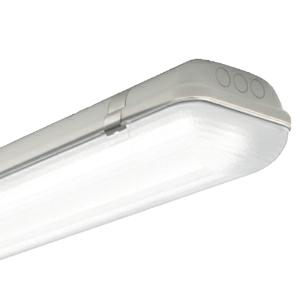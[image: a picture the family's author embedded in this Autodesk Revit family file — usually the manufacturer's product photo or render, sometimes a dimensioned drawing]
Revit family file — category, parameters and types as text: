
# Revit family: 3f_filippi_-_3f_linda_soft_3f_filippi_-_58737_-_3f_linda_led_soft_2x24w_l1270
name_source: partatom
category: Lighting Fixtures
units: mm (PartAtom-declared; Revit-internal decimal feet)

## family parameters
Cut with Voids When Loaded = No
Host = Face
Light Source = No
Part Type = Normal
Room Calculation Point = No
Round Connector Dimension = Use Diameter
Shared = No

## types (1)
- 3F Filippi - 3F Linda Soft (1 x LED, 7156 lm, 54.5 W, 4000 K)
    Apparent Load = 55 VA
    Approval mark = CE
    CIE Flux Codes = 42 72 91 93 100
    Color Rendering = 80
    Color Temperature = 4000 K
    Control Gear = Electronic ballast
    Default Elevation = 1800 mm
    Description = ILLUMINOTECHNICAL
Luminous efficiency 100% (DLOR 93%, ULOR 7%).
Initial luminous flux of the luminaire 7156 lm.
Direct symmetric distribution.
Installation Interdistance Transv.D = 1.35 x hu - Long.D = 1.24 x hu.
Tabular UGR (CIE 117 - 4H-8H; S=0.25H; 70/50/20): RUG 24.6 - 22.6.
Beam angle: 131° - 111°.
Luminous efficacy 131 lm/W.
Lifetime (L93/B10): 30000 h. (tq+25°C)
Lifetime (L90/B10): 50000 h. (tq+25°C)
Lifetime (L85/B10): 80000 h. (tq+25°C)
Lifetime (L80/B10): 100000 h. (tq+25°C)
Lifetime (L85/B10): 50000 h. (tq+35°C)
Sudden decreased luminous flux after 50000 hours: 0% (C0).
Photobiological safety in compliance with IEC/TR 62778: RG0 risk exempt, (IEC 62471).
In compliance with IEC/EN 62722-2-1 - IEC/EN 62717 standards.

SOURCE
2 linear LED modules 24W/840.
Energy efficiency class (UE 2019/2020 - UE 2019/2015): D.
CIE 13.3 Colour rendering index: CRI >80 (R9 <50%).
IES TM-30 Fidelity Index: Rf = 84 Rg = 95.
CCT nominal colour temperature 4000 K.
Colour initial tolerance (MacAdam): SDCM 3.

MECHANICAL
Self-extinguishing V2 polycarbonate housing, injection moulded, RAL 7035 grey.
Ecologic anti-aging injected sealing gasket.
Soft opal diffuser in self-extinguishing V2 polycarbonate, photo-engraved interior, UV stabilised, injection moulded.
Gear-holder reflector in hot-dip galvanised steel, painted with white polyester base.
Snug fit safety snap-lock clips for diffuser mounting in stainless steel, screwdriver opening.
Fixing brackets in stainless steel.
Possibility for technicians to access the interior of the luminaire.
Luminaire with limited surface temperature. - D - (EN 60598-2-24)
Dimensions: 1270x160 mm, height 100 mm. Weight 2.57 kg.
IP66 protection degree.
Mechanical strength to impacts IK10 (20 joule).
Glow-wire test resistance 850°C.

ELECTRICAL
Halogen Free electronic wiring 230V-50/60Hz, power factor 0.97, THD <25%, constant output current, SELV, class I, 1 driver.
Power of the luminaire 54.5 W.
ENEC - CE.
SAFE FLICKER: PstLM=<1 and SVM=<0.4 (IEC TR 61547-1 and IEC TR 63158), to ensure a more comfortable and safe light.
Luminaire compliant with EN 60598-2-22 for power supply from a centralised emergency system CPSS (Central Power Supply System), not incorporated in the luminaire - high risk areas excluded. The default power and flux are 100% in AC and 100% in DC.
Ambient temperature from -20°C to +35°C.
Temperature class T6 max 85°C.
Relative humidity UR: <85%.

INSTALLATION
Ceiling / Suspended / Wall.
All accessories dedicated to this product are available on the Catalog and on our website www.3F-Filippi.com.

APPLICATIONS
Suitable product for food production plants (HACCP), IFS (Food Version 6), BRC (GSFS Food Version 7).
Dry, dusty indoor environments, subject to occasional water splashes.
Luminaires designed for diffuse direct/indirect lighting suitable to provide optimum visual comfort.
Transit areas, stairwells.
Virtually shatterproof polycarbonate compatibly with the fumes / atmospheres that compromise the elasticity of plastic materials.
Suitable for illumination of public car parks and parking grounds referred to DIN 67528:2018-04.

WARNING
Fixture not suitable for cold stores with an ambient temperature <0°C and/or relative humidity >85%.
Luminaire designed for disposal/recycling at end-of-life.
Replaceable (LED only) light source by a professional. Replaceable control gear by a professional.
    Height = 100 mm  [stored 0.328084 ft]
    Lamp = 1 x LED
    Lamp Light Flux = 7156 lm
    Lamp Power = 54.5 W
    Lamp count = 1
    Length = 1270 mm
    Lifetime = 50000 h
    Luminous efficacy = 131 lm/W
    Manufacturer = 3F Filippi
    ModVariant = No
    Model = 3F Filippi - 58737 - 3F Linda LED Soft 2x24W L1270
    Mounting Place = Ceiling
    Mounting Type = Pendant
    Number of Poles = 1
    OnlyDefault = Yes
    Power Factor = 1
    Product Name = 3F Filippi - 3F Linda Soft
    Product group = pendant luminaire
    ProductGroupID = 9
    Protection Class = Protection class I
    Protection Degree = IP 66
    RLX_Detail_Level = 1
    RLX_Emergency_Light_Flux = 0 lm
    RLX_Emergency_Type = 0
    RLX_Emergency_Type_DB = No
    RlxData = <blob elided: 69201 chars, md5=4299bdd8>
    Socket = socket
    Standby Power = 0 W
    System Light Flux = 7156 lm
    System Power = 55 W
    Type Comments = Product without accessories
    Type Image = 3ffilippi_3f_linda_led_soft_2x.jpg
    URL = http://relux.com
    VarID = ---
    Voltage = 0 V
    Weight = 0.00 kg
    Width = 160 mm

note: [stored X ft] marks values corroborated as IEEE doubles in the binary element streams (Revit-internal decimal feet)

## geometry (parser evidence)
native form markers: Blend x4, Sweep x12
no freeform markers — native parametric forms only
